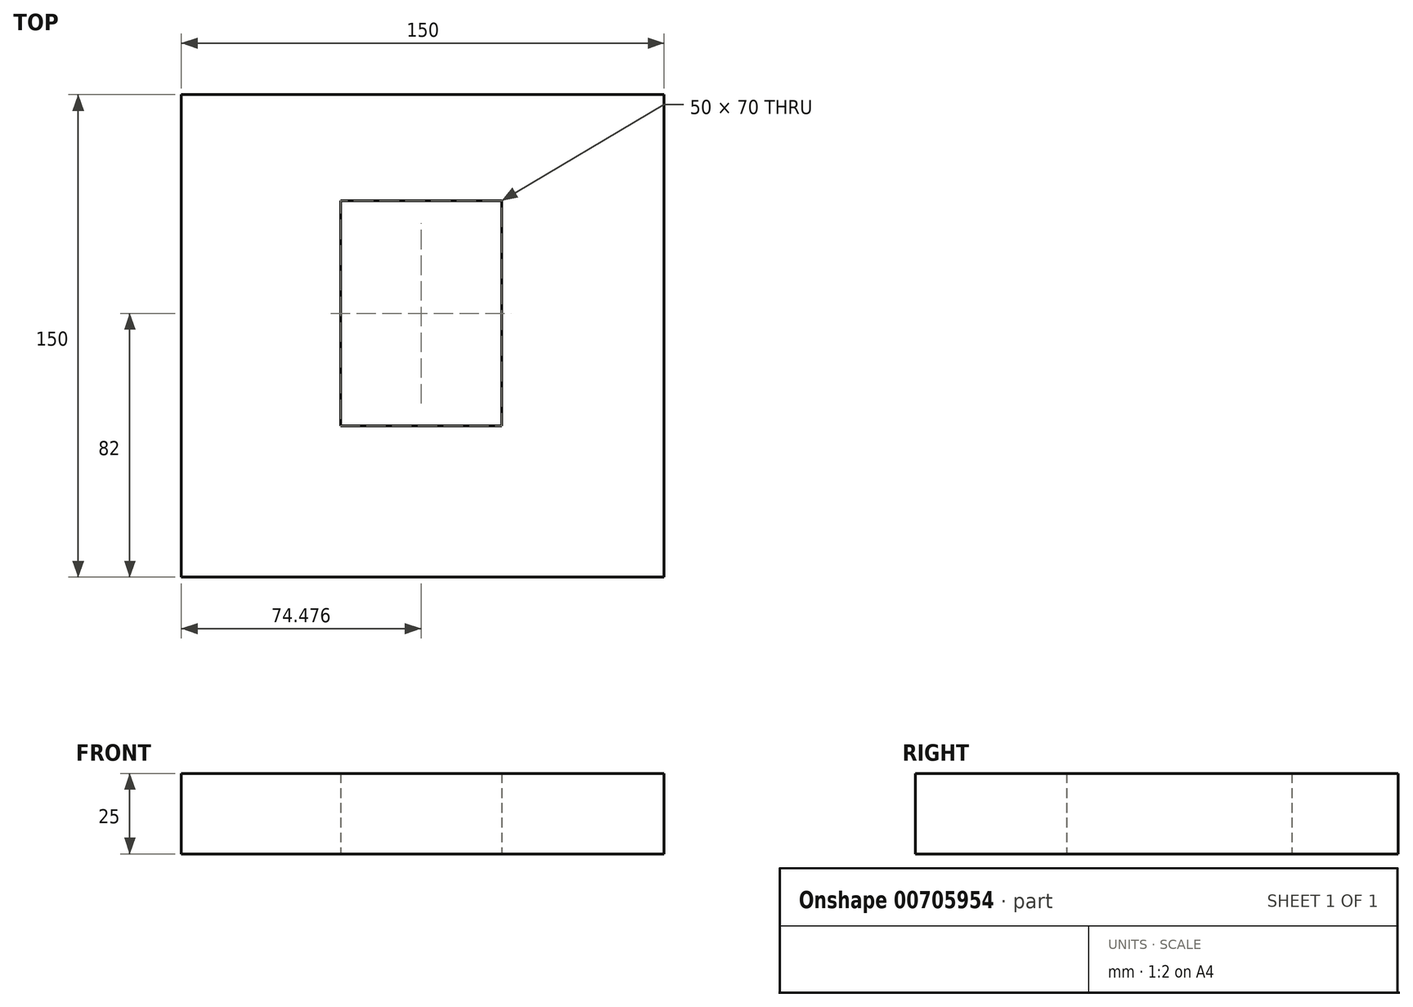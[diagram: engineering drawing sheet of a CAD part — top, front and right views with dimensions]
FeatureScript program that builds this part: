
annotation { "Feature Type Name" : "Feature", "Feature Type Description" : "" }
export const myFeature = defineFeature(function(context is Context, id is Id, definition is map)
    precondition{}
    {
        {
            var Q0;
            Q0=qCreatedBy(makeId("Top.planeOp"),FACE);
            var sketch = newSketch(context, id + "F0", { "sketchPlane" : qUnion([Q0])});
            skLineSegment(sketch, "E0.bottom", {"start": v(0, 0) * mm, "end": v(150, 0) * mm});
            skLineSegment(sketch, "E0.top", {"start": v(0, -150) * mm, "end": v(150, -150) * mm});
            skLineSegment(sketch, "E0.left", {"start": v(0, 0) * mm, "end": v(0, -150) * mm});
            skLineSegment(sketch, "E0.right", {"start": v(150, 0) * mm, "end": v(150, -150) * mm});
            skLineSegment(sketch, "E1.bottom", {"start": v(49.48, -33) * mm, "end": v(99.48, -33) * mm});
            skLineSegment(sketch, "E1.top", {"start": v(49.48, -103) * mm, "end": v(99.48, -103) * mm});
            skLineSegment(sketch, "E1.left", {"start": v(49.48, -33) * mm, "end": v(49.48, -103) * mm});
            skLineSegment(sketch, "E1.right", {"start": v(99.48, -33) * mm, "end": v(99.48, -103) * mm});
            skSolve(sketch);
        }
        {
            var Q0;
            Q0 = qSketchRegion(id + "F0", true);
            extrude(context, id + "F1", {"entities" : qUnion([Q0]), "depth" : 25 * mm, "offsetDistance" : 25 * mm});
        }
    });
